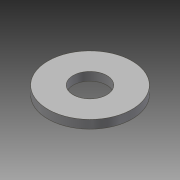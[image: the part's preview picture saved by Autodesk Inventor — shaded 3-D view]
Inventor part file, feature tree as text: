
AUTODESK INVENTOR PART (.ipt)
format: ipt  version: 2014 SP1 (Build 180222100, 222)  size: 80,896 bytes
history: native  units: in
note: dims shown in document units (in); Inventor stores cm internally (conversion verified against a paired STEP export)
features: extrude x1, sketch x1
ambient origin geometry x8: Origin, YZ Plane, XZ Plane, XY Plane, X Axis, Y Axis, Z Axis, Center Point
bodies: Solid1 (feature_tree)
feature tree (2):
  extrude  "Extrusion1"  Depth=0.0312in
  sketch  "Sketch1"  dims[d0=0.125in d1=0.3125in d2=0.0312in d3=0.0in]
